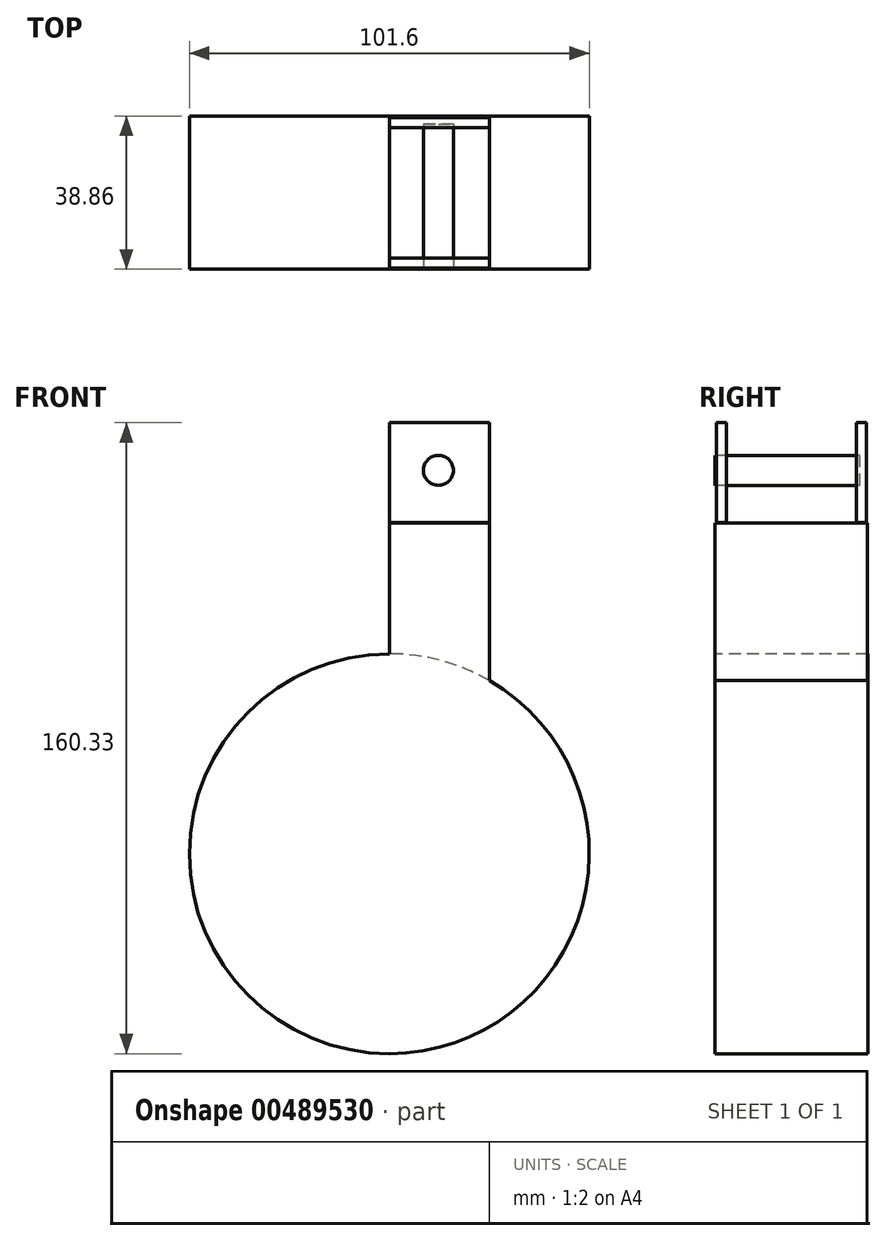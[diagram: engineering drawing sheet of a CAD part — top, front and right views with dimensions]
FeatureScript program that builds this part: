
annotation { "Feature Type Name" : "Feature", "Feature Type Description" : "" }
export const myFeature = defineFeature(function(context is Context, id is Id, definition is map)
    precondition{}
    {
        {
            var Q0;
            Q0=qCreatedBy(makeId("Front.planeOp"),FACE);
            var sketch = newSketch(context, id + "F0", { "sketchPlane" : qUnion([Q0])});
            skCircle(sketch, "E0", {"center": v(0, 0) * mm, "radius": 50.8 * mm});
            skSolve(sketch);
        }
        {
            var Q0;
            Q0 = qSketchRegion(id + "F0", true);
            extrude(context, id + "F1", {"entities" : qUnion([Q0]), "oppositeDirection" : true, "depth" : 38.86 * mm});
        }
        {
            var Q0;
            Q0=qCreatedBy(makeId("Right.planeOp"),FACE);
            var sketch = newSketch(context, id + "F2", { "sketchPlane" : qUnion([Q0])});
            skLineSegment(sketch, "E1.bottom", {"start": v(0, 83.98) * mm, "end": v(38.71, 83.98) * mm});
            skLineSegment(sketch, "E1.top", {"start": v(0, 4.06) * mm, "end": v(38.71, 4.06) * mm});
            skLineSegment(sketch, "E1.left", {"start": v(0, 83.98) * mm, "end": v(0, 4.06) * mm});
            skLineSegment(sketch, "E1.right", {"start": v(38.71, 83.98) * mm, "end": v(38.71, 4.06) * mm});
            skSolve(sketch);
        }
        {
            var Q0;
            Q0=sQuery(id+"F2.wireOp",EDGE,"E1.right");
            var Q1;
            Q1=sQuery(id+"F2.wireOp",EDGE,"E1.bottom");
            var Q2;
            Q2=sQuery(id+"F2.wireOp",EDGE,"E1.left");
            var Q3;
            Q3=sQuery(id+"F2.wireOp",EDGE,"E1.top");
            extrude(context, id + "F3", {"bodyType" : ToolBodyType.SURFACE, "surfaceEntities" : qUnion([Q0, Q1, Q2, Q3]), "depth" : 25.4 * mm});
        }
        {
            var Q0;
            Q0=makeQuery(id+"F2.imprint","IMPRINT",FACE,{"disambiguationData":[TD([[makeQuery(id+"F2.imprint","IMPRINT",EDGE,{"derivedFrom":sQuery(id+"F2.wireOp",EDGE,"E1.bottom")}),-1.0]])]});
            extrude(context, id + "F4", {"entities" : qUnion([Q0]), "operationType" : NewBodyOperationType.ADD, "depth" : 25.4 * mm});
        }
        {
            var Q0;
            Q0=qCreatedBy(makeId("Right.planeOp"),FACE);
            var sketch = newSketch(context, id + "F5", { "sketchPlane" : qUnion([Q0])});
            skLineSegment(sketch, "E2.bottom", {"start": v(0.3, 84.13) * mm, "end": v(2.83, 84.13) * mm});
            skLineSegment(sketch, "E2.top", {"start": v(0.3, 109.53) * mm, "end": v(2.83, 109.53) * mm});
            skLineSegment(sketch, "E2.left", {"start": v(0.3, 84.13) * mm, "end": v(0.3, 109.53) * mm});
            skLineSegment(sketch, "E2.right", {"start": v(2.83, 84.13) * mm, "end": v(2.83, 109.53) * mm});
            skLineSegment(sketch, "E3.bottom", {"start": v(35.9, 84.13) * mm, "end": v(38.44, 84.13) * mm});
            skLineSegment(sketch, "E3.top", {"start": v(35.9, 109.53) * mm, "end": v(38.44, 109.53) * mm});
            skLineSegment(sketch, "E3.left", {"start": v(38.44, 84.13) * mm, "end": v(38.44, 109.53) * mm});
            skLineSegment(sketch, "E3.right", {"start": v(35.9, 84.13) * mm, "end": v(35.9, 109.53) * mm});
            skSolve(sketch);
        }
        {
            var Q0;
            Q0=makeQuery(id+"F5.imprint","IMPRINT",FACE,{"disambiguationData":[TD([[makeQuery(id+"F5.imprint","IMPRINT",EDGE,{"derivedFrom":sQuery(id+"F5.wireOp",EDGE,"E2.bottom")}),1.0]])]});
            var Q1;
            Q1=makeQuery(id+"F5.imprint","IMPRINT",FACE,{"disambiguationData":[TD([[makeQuery(id+"F5.imprint","IMPRINT",EDGE,{"derivedFrom":sQuery(id+"F5.wireOp",EDGE,"E3.bottom")}),1.0]])]});
            extrude(context, id + "F6", {"entities" : qUnion([Q0, Q1]), "depth" : 25.4 * mm});
        }
        {
            var Q0;
            Q0=qCreatedBy(makeId("Front.planeOp"),FACE);
            var sketch = newSketch(context, id + "F7", { "sketchPlane" : qUnion([Q0])});
            skCircle(sketch, "E4", {"center": v(12.49, 97.4) * mm, "radius": 3.81 * mm});
            skSolve(sketch);
        }
        {
            var Q0;
            Q0 = qSketchRegion(id + "F7", true);
            extrude(context, id + "F8", {"entities" : qUnion([Q0]), "oppositeDirection" : true, "depth" : 36.83 * mm});
        }
    });
